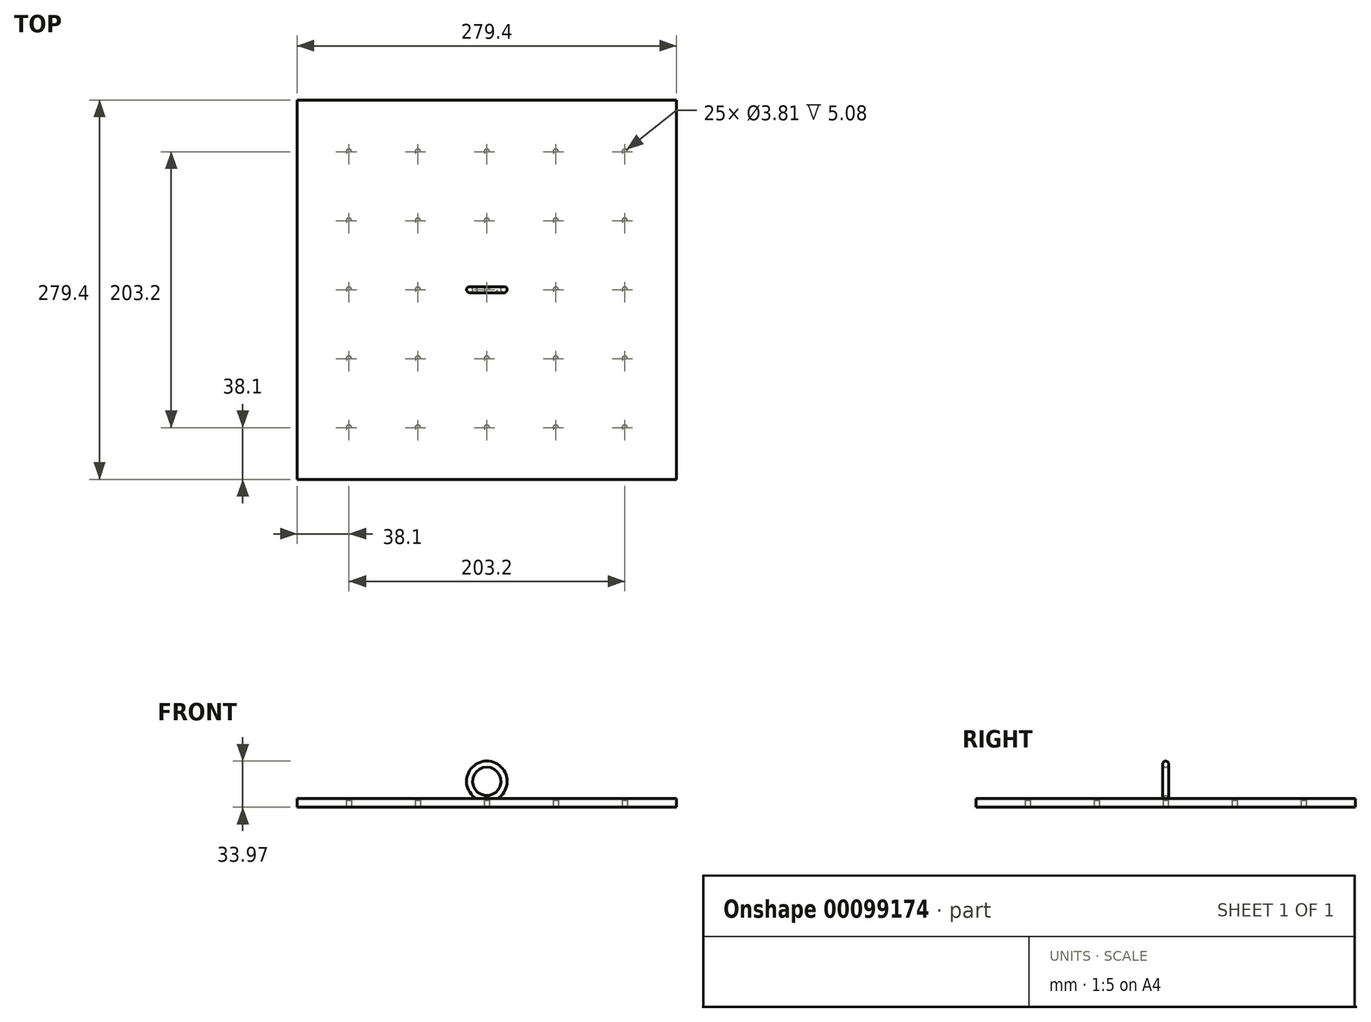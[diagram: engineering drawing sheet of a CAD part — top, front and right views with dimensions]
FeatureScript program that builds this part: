
annotation { "Feature Type Name" : "Feature", "Feature Type Description" : "" }
export const myFeature = defineFeature(function(context is Context, id is Id, definition is map)
    precondition{}
    {
        {
            var Q0;
            Q0=qCreatedBy(makeId("Top.planeOp"),FACE);
            var sketch = newSketch(context, id + "F0", { "sketchPlane" : qUnion([Q0])});
            skLineSegment(sketch, "E0.bottom", {"start": v(0, 0) * mm, "end": v(279.4, 0) * mm});
            skLineSegment(sketch, "E0.top", {"start": v(0, 279.4) * mm, "end": v(279.4, 279.4) * mm});
            skLineSegment(sketch, "E0.left", {"start": v(0, 0) * mm, "end": v(0, 279.4) * mm});
            skLineSegment(sketch, "E0.right", {"start": v(279.4, 0) * mm, "end": v(279.4, 279.4) * mm});
            skSolve(sketch);
        }
        {
            var Q0;
            Q0=makeQuery(id+"F0.imprint","IMPRINT",FACE,{"disambiguationData":[TD([[makeQuery(id+"F0.imprint","IMPRINT",EDGE,{"derivedFrom":sQuery(id+"F0.wireOp",EDGE,"E0.bottom")}),1.0]])]});
            extrude(context, id + "F1", {"entities" : qUnion([Q0]), "depth" : 6.35 * mm});
        }
        {
            var Q0;
            Q0=qCreatedBy(makeId("Front.planeOp"),FACE);
            cPlane(context, id + "F2", {"entities" : qUnion([Q0]), "cplaneType" : CPlaneType.OFFSET, "offset" : 139.7 * mm, "oppositeDirection" : true, "width" : 152.4 * mm, "height" : 152.4 * mm});
        }
        {
            var Q0;
            Q0=qCreatedBy(id+"F2.planeOp",FACE);
            var sketch = newSketch(context, id + "F3", { "sketchPlane" : qUnion([Q0])});
            skLineSegment(sketch, "E1", {"start": v(0, 0) * mm, "end": v(139.7, 0) * mm, "construction": true});
            skLineSegment(sketch, "E2", {"start": v(139.7, 0) * mm, "end": v(139.7, 19.05) * mm, "construction": true});
            skCircle(sketch, "E3", {"center": v(139.7, 19.05) * mm, "radius": 12.7 * mm});
            skSolve(sketch);
        }
        {
            var Q0;
            Q0=qCreatedBy(makeId("Right.planeOp"),FACE);
            cPlane(context, id + "F4", {"entities" : qUnion([Q0]), "cplaneType" : CPlaneType.OFFSET, "offset" : 139.7 * mm, "width" : 152.4 * mm, "height" : 152.4 * mm});
        }
        {
            var Q0;
            Q0=qCreatedBy(id+"F4.planeOp",FACE);
            var sketch = newSketch(context, id + "F5", { "sketchPlane" : qUnion([Q0])});
            skLineSegment(sketch, "E4", {"start": v(0, 0) * mm, "end": v(139.7, 0) * mm, "construction": true});
            skLineSegment(sketch, "E5", {"start": v(139.7, 0) * mm, "end": v(139.7, 6.35) * mm, "construction": true});
            skCircle(sketch, "E6", {"center": v(139.7, 6.35) * mm, "radius": 2.22 * mm});
            skSolve(sketch);
        }
        {
            var Q0;
            Q0=makeQuery(id+"F5.imprint","IMPRINT",FACE,{"disambiguationData":[TD([[makeQuery(id+"F5.imprint","IMPRINT",EDGE,{"derivedFrom":sQuery(id+"F5.wireOp",EDGE,"E6")}),1.0]])]});
            var Q1;
            Q1=sQuery(id+"F3.wireOp",EDGE,"E3");
            sweep(context, id + "F6", {"operationType" : NewBodyOperationType.ADD, "profiles" : qUnion([Q0]), "path" : qUnion([Q1])});
        }
        {
            var Q0;
            Q0=makeQuery(id+"F1.opExtrude","CAP_FACE",FACE,{"disambiguationData":[OSD([sQuery(id+"F0.wireOp",EDGE,"E0.bottom"),sQuery(id+"F0.wireOp",EDGE,"E0.top"),sQuery(id+"F0.wireOp",EDGE,"E0.left"),sQuery(id+"F0.wireOp",EDGE,"E0.right")])],"isStart":true});
            var sketch = newSketch(context, id + "F7", { "sketchPlane" : qUnion([Q0])});
            skLineSegment(sketch, "E7", {"start": v(0, 0) * mm, "end": v(38.1, 0) * mm, "construction": true});
            skLineSegment(sketch, "E8", {"start": v(38.1, 0) * mm, "end": v(38.1, -38.1) * mm, "construction": true});
            skCircle(sketch, "E9", {"center": v(38.1, -38.1) * mm, "radius": 22.23 * mm, "construction": true});
            skCircle(sketch, "E10.1.0.0", {"center": v(88.9, -38.1) * mm, "radius": 22.23 * mm, "construction": true});
            skCircle(sketch, "E10.2.0.0", {"center": v(139.7, -38.1) * mm, "radius": 22.23 * mm, "construction": true});
            skCircle(sketch, "E10.3.0.0", {"center": v(190.5, -38.1) * mm, "radius": 22.23 * mm, "construction": true});
            skCircle(sketch, "E10.4.0.0", {"center": v(241.3, -38.1) * mm, "radius": 22.23 * mm, "construction": true});
            skLineSegment(sketch, "E10.direction1", {"start": v(38.1, -38.1) * mm, "end": v(88.9, -38.1) * mm, "construction": true});
            skCircle(sketch, "E11.1.0.0", {"center": v(38.1, -88.9) * mm, "radius": 22.23 * mm, "construction": true});
            skCircle(sketch, "E11.1.0.1", {"center": v(88.9, -88.9) * mm, "radius": 22.23 * mm, "construction": true});
            skCircle(sketch, "E11.1.0.2", {"center": v(139.7, -88.9) * mm, "radius": 22.23 * mm, "construction": true});
            skCircle(sketch, "E11.1.0.3", {"center": v(190.5, -88.9) * mm, "radius": 22.23 * mm, "construction": true});
            skCircle(sketch, "E11.1.0.4", {"center": v(241.3, -88.9) * mm, "radius": 22.23 * mm, "construction": true});
            skCircle(sketch, "E11.2.0.0", {"center": v(38.1, -139.7) * mm, "radius": 22.23 * mm, "construction": true});
            skCircle(sketch, "E11.2.0.1", {"center": v(88.9, -139.7) * mm, "radius": 22.23 * mm, "construction": true});
            skCircle(sketch, "E11.2.0.2", {"center": v(139.7, -139.7) * mm, "radius": 22.23 * mm, "construction": true});
            skCircle(sketch, "E11.2.0.3", {"center": v(190.5, -139.7) * mm, "radius": 22.23 * mm, "construction": true});
            skCircle(sketch, "E11.2.0.4", {"center": v(241.3, -139.7) * mm, "radius": 22.23 * mm, "construction": true});
            skCircle(sketch, "E11.3.0.0", {"center": v(38.1, -190.5) * mm, "radius": 22.23 * mm, "construction": true});
            skCircle(sketch, "E11.3.0.1", {"center": v(88.9, -190.5) * mm, "radius": 22.23 * mm, "construction": true});
            skCircle(sketch, "E11.3.0.2", {"center": v(139.7, -190.5) * mm, "radius": 22.23 * mm, "construction": true});
            skCircle(sketch, "E11.3.0.3", {"center": v(190.5, -190.5) * mm, "radius": 22.23 * mm, "construction": true});
            skCircle(sketch, "E11.3.0.4", {"center": v(241.3, -190.5) * mm, "radius": 22.23 * mm, "construction": true});
            skCircle(sketch, "E11.4.0.0", {"center": v(38.1, -241.3) * mm, "radius": 22.23 * mm, "construction": true});
            skCircle(sketch, "E11.4.0.1", {"center": v(88.9, -241.3) * mm, "radius": 22.23 * mm, "construction": true});
            skCircle(sketch, "E11.4.0.2", {"center": v(139.7, -241.3) * mm, "radius": 22.23 * mm, "construction": true});
            skCircle(sketch, "E11.4.0.3", {"center": v(190.5, -241.3) * mm, "radius": 22.23 * mm, "construction": true});
            skCircle(sketch, "E11.4.0.4", {"center": v(241.3, -241.3) * mm, "radius": 22.23 * mm, "construction": true});
            skLineSegment(sketch, "E11.direction1", {"start": v(38.1, -38.1) * mm, "end": v(38.1, -88.9) * mm, "construction": true});
            skCircle(sketch, "E12", {"center": v(38.1, -38.1) * mm, "radius": 1.9 * mm});
            skCircle(sketch, "E13.0.1.0", {"center": v(38.1, -88.9) * mm, "radius": 1.9 * mm});
            skCircle(sketch, "E13.0.2.0", {"center": v(38.1, -139.7) * mm, "radius": 1.9 * mm});
            skCircle(sketch, "E13.0.3.0", {"center": v(38.1, -190.5) * mm, "radius": 1.9 * mm});
            skCircle(sketch, "E13.0.4.0", {"center": v(38.1, -241.3) * mm, "radius": 1.9 * mm});
            skCircle(sketch, "E13.1.0.0", {"center": v(88.9, -38.1) * mm, "radius": 1.9 * mm});
            skCircle(sketch, "E13.1.1.0", {"center": v(88.9, -88.9) * mm, "radius": 1.9 * mm});
            skCircle(sketch, "E13.1.2.0", {"center": v(88.9, -139.7) * mm, "radius": 1.9 * mm});
            skCircle(sketch, "E13.1.3.0", {"center": v(88.9, -190.5) * mm, "radius": 1.9 * mm});
            skCircle(sketch, "E13.1.4.0", {"center": v(88.9, -241.3) * mm, "radius": 1.9 * mm});
            skCircle(sketch, "E13.2.0.0", {"center": v(139.7, -38.1) * mm, "radius": 1.9 * mm});
            skCircle(sketch, "E13.2.1.0", {"center": v(139.7, -88.9) * mm, "radius": 1.9 * mm});
            skCircle(sketch, "E13.2.2.0", {"center": v(139.7, -139.7) * mm, "radius": 1.9 * mm});
            skCircle(sketch, "E13.2.3.0", {"center": v(139.7, -190.5) * mm, "radius": 1.9 * mm});
            skCircle(sketch, "E13.2.4.0", {"center": v(139.7, -241.3) * mm, "radius": 1.9 * mm});
            skCircle(sketch, "E13.3.0.0", {"center": v(190.5, -38.1) * mm, "radius": 1.9 * mm});
            skCircle(sketch, "E13.3.1.0", {"center": v(190.5, -88.9) * mm, "radius": 1.9 * mm});
            skCircle(sketch, "E13.3.2.0", {"center": v(190.5, -139.7) * mm, "radius": 1.9 * mm});
            skCircle(sketch, "E13.3.3.0", {"center": v(190.5, -190.5) * mm, "radius": 1.9 * mm});
            skCircle(sketch, "E13.3.4.0", {"center": v(190.5, -241.3) * mm, "radius": 1.9 * mm});
            skCircle(sketch, "E13.4.0.0", {"center": v(241.3, -38.1) * mm, "radius": 1.9 * mm});
            skCircle(sketch, "E13.4.1.0", {"center": v(241.3, -88.9) * mm, "radius": 1.9 * mm});
            skCircle(sketch, "E13.4.2.0", {"center": v(241.3, -139.7) * mm, "radius": 1.9 * mm});
            skCircle(sketch, "E13.4.3.0", {"center": v(241.3, -190.5) * mm, "radius": 1.9 * mm});
            skCircle(sketch, "E13.4.4.0", {"center": v(241.3, -241.3) * mm, "radius": 1.9 * mm});
            skSolve(sketch);
        }
        {
            var Q0;
            Q0=makeQuery(id+"F7.imprint","IMPRINT",FACE,{"disambiguationData":[TD([[makeQuery(id+"F7.imprint","IMPRINT",EDGE,{"derivedFrom":sQuery(id+"F7.wireOp",EDGE,"E12")}),1.0]])]});
            var Q1;
            Q1=makeQuery(id+"F7.imprint","IMPRINT",FACE,{"disambiguationData":[TD([[makeQuery(id+"F7.imprint","IMPRINT",EDGE,{"derivedFrom":sQuery(id+"F7.wireOp",EDGE,"E13.1.0.0")}),1.0]])]});
            var Q2;
            Q2=makeQuery(id+"F7.imprint","IMPRINT",FACE,{"disambiguationData":[TD([[makeQuery(id+"F7.imprint","IMPRINT",EDGE,{"derivedFrom":sQuery(id+"F7.wireOp",EDGE,"E13.2.0.0")}),1.0]])]});
            var Q3;
            Q3=makeQuery(id+"F7.imprint","IMPRINT",FACE,{"disambiguationData":[TD([[makeQuery(id+"F7.imprint","IMPRINT",EDGE,{"derivedFrom":sQuery(id+"F7.wireOp",EDGE,"E13.4.0.0")}),1.0]])]});
            var Q4;
            Q4=makeQuery(id+"F7.imprint","IMPRINT",FACE,{"disambiguationData":[TD([[makeQuery(id+"F7.imprint","IMPRINT",EDGE,{"derivedFrom":sQuery(id+"F7.wireOp",EDGE,"E13.3.0.0")}),1.0]])]});
            var Q5;
            Q5=makeQuery(id+"F7.imprint","IMPRINT",FACE,{"disambiguationData":[TD([[makeQuery(id+"F7.imprint","IMPRINT",EDGE,{"derivedFrom":sQuery(id+"F7.wireOp",EDGE,"E13.0.1.0")}),1.0]])]});
            var Q6;
            Q6=makeQuery(id+"F7.imprint","IMPRINT",FACE,{"disambiguationData":[TD([[makeQuery(id+"F7.imprint","IMPRINT",EDGE,{"derivedFrom":sQuery(id+"F7.wireOp",EDGE,"E13.1.1.0")}),1.0]])]});
            var Q7;
            Q7=makeQuery(id+"F7.imprint","IMPRINT",FACE,{"disambiguationData":[TD([[makeQuery(id+"F7.imprint","IMPRINT",EDGE,{"derivedFrom":sQuery(id+"F7.wireOp",EDGE,"E13.2.1.0")}),1.0]])]});
            var Q8;
            Q8=makeQuery(id+"F7.imprint","IMPRINT",FACE,{"disambiguationData":[TD([[makeQuery(id+"F7.imprint","IMPRINT",EDGE,{"derivedFrom":sQuery(id+"F7.wireOp",EDGE,"E13.3.1.0")}),1.0]])]});
            var Q9;
            Q9=makeQuery(id+"F7.imprint","IMPRINT",FACE,{"disambiguationData":[TD([[makeQuery(id+"F7.imprint","IMPRINT",EDGE,{"derivedFrom":sQuery(id+"F7.wireOp",EDGE,"E13.4.1.0")}),1.0]])]});
            var Q10;
            Q10=makeQuery(id+"F7.imprint","IMPRINT",FACE,{"disambiguationData":[TD([[makeQuery(id+"F7.imprint","IMPRINT",EDGE,{"derivedFrom":sQuery(id+"F7.wireOp",EDGE,"E13.0.2.0")}),1.0]])]});
            var Q11;
            Q11=makeQuery(id+"F7.imprint","IMPRINT",FACE,{"disambiguationData":[TD([[makeQuery(id+"F7.imprint","IMPRINT",EDGE,{"derivedFrom":sQuery(id+"F7.wireOp",EDGE,"E13.1.2.0")}),1.0]])]});
            var Q12;
            Q12=makeQuery(id+"F7.imprint","IMPRINT",FACE,{"disambiguationData":[TD([[makeQuery(id+"F7.imprint","IMPRINT",EDGE,{"derivedFrom":sQuery(id+"F7.wireOp",EDGE,"E13.2.2.0")}),1.0]])]});
            var Q13;
            Q13=makeQuery(id+"F7.imprint","IMPRINT",FACE,{"disambiguationData":[TD([[makeQuery(id+"F7.imprint","IMPRINT",EDGE,{"derivedFrom":sQuery(id+"F7.wireOp",EDGE,"E13.3.2.0")}),1.0]])]});
            var Q14;
            Q14=makeQuery(id+"F7.imprint","IMPRINT",FACE,{"disambiguationData":[TD([[makeQuery(id+"F7.imprint","IMPRINT",EDGE,{"derivedFrom":sQuery(id+"F7.wireOp",EDGE,"E13.4.2.0")}),1.0]])]});
            var Q15;
            Q15=makeQuery(id+"F7.imprint","IMPRINT",FACE,{"disambiguationData":[TD([[makeQuery(id+"F7.imprint","IMPRINT",EDGE,{"derivedFrom":sQuery(id+"F7.wireOp",EDGE,"E13.4.3.0")}),1.0]])]});
            var Q16;
            Q16=makeQuery(id+"F7.imprint","IMPRINT",FACE,{"disambiguationData":[TD([[makeQuery(id+"F7.imprint","IMPRINT",EDGE,{"derivedFrom":sQuery(id+"F7.wireOp",EDGE,"E13.3.3.0")}),1.0]])]});
            var Q17;
            Q17=makeQuery(id+"F7.imprint","IMPRINT",FACE,{"disambiguationData":[TD([[makeQuery(id+"F7.imprint","IMPRINT",EDGE,{"derivedFrom":sQuery(id+"F7.wireOp",EDGE,"E13.2.3.0")}),1.0]])]});
            var Q18;
            Q18=makeQuery(id+"F7.imprint","IMPRINT",FACE,{"disambiguationData":[TD([[makeQuery(id+"F7.imprint","IMPRINT",EDGE,{"derivedFrom":sQuery(id+"F7.wireOp",EDGE,"E13.1.3.0")}),1.0]])]});
            var Q19;
            Q19=makeQuery(id+"F7.imprint","IMPRINT",FACE,{"disambiguationData":[TD([[makeQuery(id+"F7.imprint","IMPRINT",EDGE,{"derivedFrom":sQuery(id+"F7.wireOp",EDGE,"E13.0.3.0")}),1.0]])]});
            var Q20;
            Q20=makeQuery(id+"F7.imprint","IMPRINT",FACE,{"disambiguationData":[TD([[makeQuery(id+"F7.imprint","IMPRINT",EDGE,{"derivedFrom":sQuery(id+"F7.wireOp",EDGE,"E13.0.4.0")}),1.0]])]});
            var Q21;
            Q21=makeQuery(id+"F7.imprint","IMPRINT",FACE,{"disambiguationData":[TD([[makeQuery(id+"F7.imprint","IMPRINT",EDGE,{"derivedFrom":sQuery(id+"F7.wireOp",EDGE,"E13.1.4.0")}),1.0]])]});
            var Q22;
            Q22=makeQuery(id+"F7.imprint","IMPRINT",FACE,{"disambiguationData":[TD([[makeQuery(id+"F7.imprint","IMPRINT",EDGE,{"derivedFrom":sQuery(id+"F7.wireOp",EDGE,"E13.2.4.0")}),1.0]])]});
            var Q23;
            Q23=makeQuery(id+"F7.imprint","IMPRINT",FACE,{"disambiguationData":[TD([[makeQuery(id+"F7.imprint","IMPRINT",EDGE,{"derivedFrom":sQuery(id+"F7.wireOp",EDGE,"E13.3.4.0")}),1.0]])]});
            var Q24;
            Q24=makeQuery(id+"F7.imprint","IMPRINT",FACE,{"disambiguationData":[TD([[makeQuery(id+"F7.imprint","IMPRINT",EDGE,{"derivedFrom":sQuery(id+"F7.wireOp",EDGE,"E13.4.4.0")}),1.0]])]});
            extrude(context, id + "F8", {"entities" : qUnion([Q0, Q1, Q2, Q3, Q4, Q5, Q6, Q7, Q8, Q9, Q10, Q11, Q12, Q13, Q14, Q15, Q16, Q17, Q18, Q19, Q20, Q21, Q22, Q23, Q24]), "operationType" : NewBodyOperationType.REMOVE, "oppositeDirection" : true, "depth" : 5.08 * mm});
        }
    });
